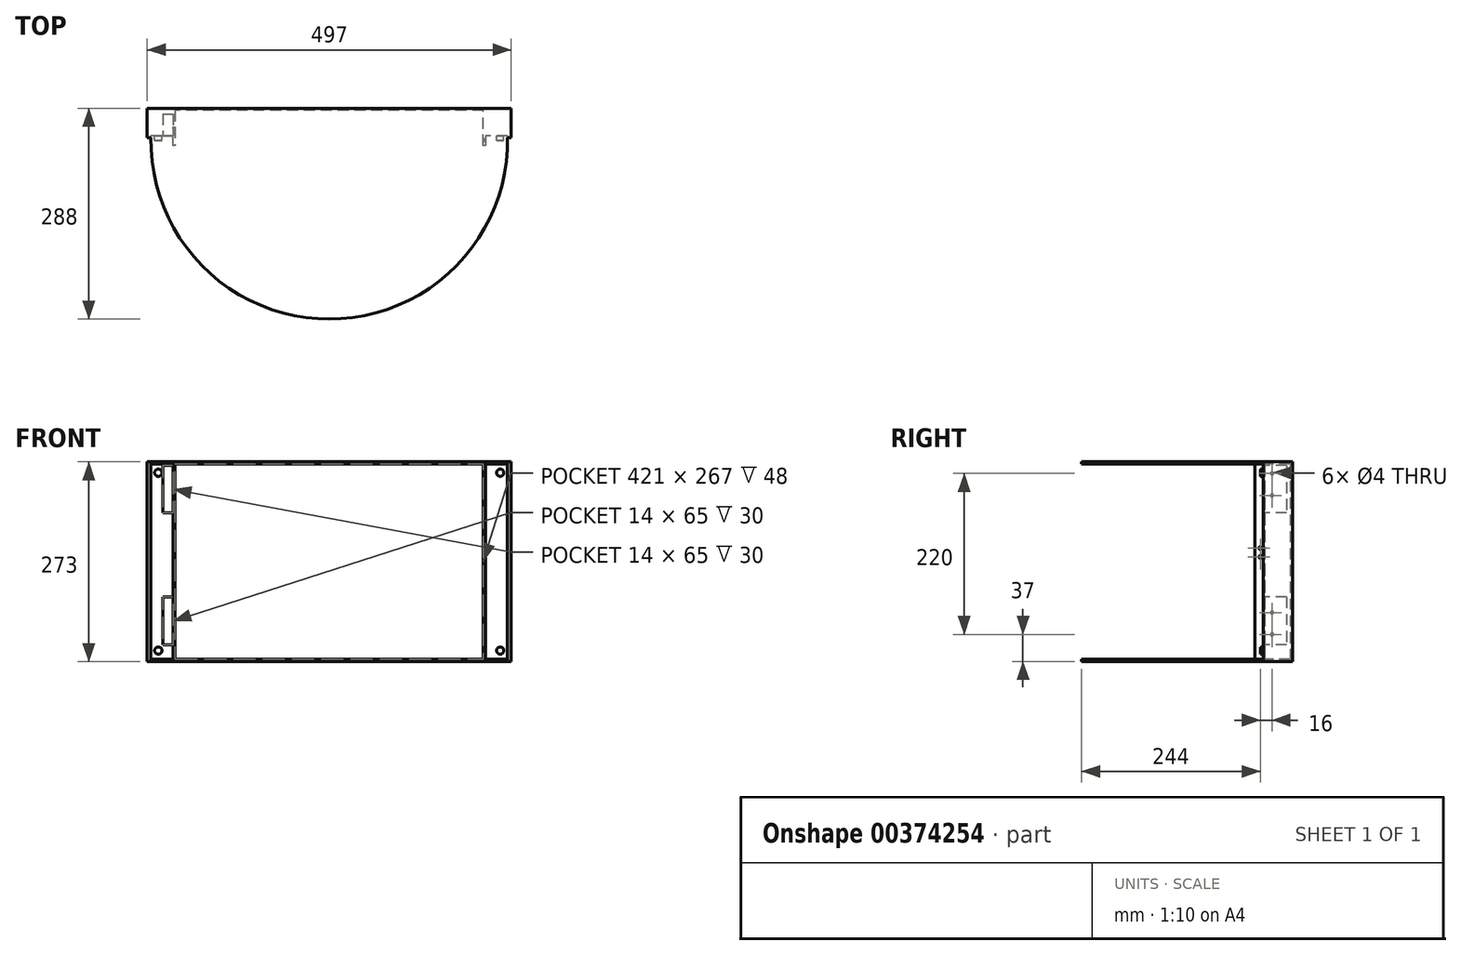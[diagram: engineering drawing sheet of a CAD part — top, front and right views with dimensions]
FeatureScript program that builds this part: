
annotation { "Feature Type Name" : "Feature", "Feature Type Description" : "" }
export const myFeature = defineFeature(function(context is Context, id is Id, definition is map)
    precondition{}
    {
        {
            var Q0;
            Q0=qCreatedBy(makeId("Top.planeOp"),FACE);
            var sketch = newSketch(context, id + "F0", { "sketchPlane" : qUnion([Q0])});
            skLineSegment(sketch, "E0", {"start": v(-248.5, 40) * mm, "end": v(248.5, 40) * mm});
            skLineSegment(sketch, "E1", {"start": v(248.5, 40) * mm, "end": v(248.5, 0) * mm});
            skLineSegment(sketch, "E2", {"start": v(248.5, 0) * mm, "end": v(243.5, 0) * mm});
            skLineSegment(sketch, "E3", {"start": v(243.5, 0) * mm, "end": v(243.5, 2) * mm});
            skLineSegment(sketch, "E4", {"start": v(243.5, 2) * mm, "end": v(213.5, 2) * mm});
            skLineSegment(sketch, "E5", {"start": v(213.5, 2) * mm, "end": v(213.5, -11) * mm});
            skLineSegment(sketch, "E6", {"start": v(213.5, -11) * mm, "end": v(210.5, -11) * mm});
            skLineSegment(sketch, "E7", {"start": v(210.5, -11) * mm, "end": v(210.5, 37) * mm});
            skLineSegment(sketch, "E8", {"start": v(210.5, 37) * mm, "end": v(-210.5, 37) * mm});
            skLineSegment(sketch, "E9", {"start": v(-210.5, 37) * mm, "end": v(-210.5, -11) * mm});
            skLineSegment(sketch, "E10", {"start": v(-210.5, -11) * mm, "end": v(-213.5, -11) * mm});
            skLineSegment(sketch, "E11", {"start": v(-213.5, -11) * mm, "end": v(-213.5, 2) * mm});
            skLineSegment(sketch, "E12", {"start": v(-213.5, 2) * mm, "end": v(-243.5, 2) * mm});
            skLineSegment(sketch, "E13", {"start": v(-243.5, 2) * mm, "end": v(-243.5, 0) * mm});
            skLineSegment(sketch, "E14", {"start": v(-243.5, 0) * mm, "end": v(-248.5, 0) * mm});
            skLineSegment(sketch, "E15", {"start": v(-248.5, 0) * mm, "end": v(-248.5, 40) * mm});
            skArc(sketch, "E16", {"start": v(-243.5, 0) * mm, "mid": v(0, -248) * mm, "end": v(243.5, 0) * mm});
            skSolve(sketch);
        }
        {
            var Q0;
            Q0=makeQuery(id+"F0.imprint","IMPRINT",FACE,{"disambiguationData":[TD([[makeQuery(id+"F0.imprint","IMPRINT",EDGE,{"derivedFrom":sQuery(id+"F0.wireOp",EDGE,"E3")}),1.0]])]});
            extrude(context, id + "F1", {"entities" : qUnion([Q0]), "depth" : 3 * mm});
        }
        {
            var Q0;
            Q0=makeQuery(id+"F0.imprint","IMPRINT",FACE,{"disambiguationData":[TD([[makeQuery(id+"F0.imprint","IMPRINT",EDGE,{"derivedFrom":sQuery(id+"F0.wireOp",EDGE,"E0")}),-1.0]])]});
            extrude(context, id + "F2", {"entities" : qUnion([Q0]), "operationType" : NewBodyOperationType.ADD, "depth" : 273 * mm});
        }
        {
            var Q0;
            Q0=makeQuery(id+"F1.opExtrude","CAP_FACE",FACE,{"disambiguationData":[OSD([sQuery(id+"F0.wireOp",EDGE,"E3"),sQuery(id+"F0.wireOp",EDGE,"E4"),sQuery(id+"F0.wireOp",EDGE,"E5"),sQuery(id+"F0.wireOp",EDGE,"E6"),sQuery(id+"F0.wireOp",EDGE,"E7"),sQuery(id+"F0.wireOp",EDGE,"E8"),sQuery(id+"F0.wireOp",EDGE,"E9"),sQuery(id+"F0.wireOp",EDGE,"E10"),sQuery(id+"F0.wireOp",EDGE,"E11"),sQuery(id+"F0.wireOp",EDGE,"E12"),sQuery(id+"F0.wireOp",EDGE,"E13"),sQuery(id+"F0.wireOp",EDGE,"E16")])],"isStart":false});
            extrude(context, id + "F3", {"entities" : qUnion([Q0]), "operationType" : NewBodyOperationType.ADD, "depth" : 270 * mm, "hasSecondDirection" : true, "secondDirectionOppositeDirection" : false, "secondDirectionDepth" : 267 * mm});
        }
        {
            var Q0;
            Q0=makeQuery(id+"F2.opExtrude","SWEPT_FACE",FACE,{"disambiguationData":[OSD([sQuery(id+"F0.wireOp",EDGE,"E12")])]});
            var sketch = newSketch(context, id + "F4", { "sketchPlane" : qUnion([Q0])});
            skLineSegment(sketch, "E17.bottom", {"start": v(-227.5, 88) * mm, "end": v(-213.5, 88) * mm});
            skLineSegment(sketch, "E17.top", {"start": v(-227.5, 23) * mm, "end": v(-213.5, 23) * mm});
            skLineSegment(sketch, "E17.left", {"start": v(-227.5, 88) * mm, "end": v(-227.5, 23) * mm});
            skLineSegment(sketch, "E17.right", {"start": v(-213.5, 88) * mm, "end": v(-213.5, 23) * mm});
            skLineSegment(sketch, "E18.bottom", {"start": v(-227.5, 268) * mm, "end": v(-213.5, 268) * mm});
            skLineSegment(sketch, "E18.top", {"start": v(-227.5, 203) * mm, "end": v(-213.5, 203) * mm});
            skLineSegment(sketch, "E18.left", {"start": v(-227.5, 268) * mm, "end": v(-227.5, 203) * mm});
            skLineSegment(sketch, "E18.right", {"start": v(-213.5, 268) * mm, "end": v(-213.5, 203) * mm});
            skCircle(sketch, "E19", {"center": v(-233.5, 258) * mm, "radius": 5 * mm});
            skCircle(sketch, "E20", {"center": v(-233.5, 15) * mm, "radius": 5 * mm});
            skCircle(sketch, "E21", {"center": v(233.5, 15) * mm, "radius": 5 * mm});
            skCircle(sketch, "E22", {"center": v(233.5, 258) * mm, "radius": 5 * mm});
            skSolve(sketch);
        }
        {
            var Q0;
            Q0=makeQuery(id+"F4.imprint","IMPRINT",FACE,{"disambiguationData":[TD([[makeQuery(id+"F4.imprint","IMPRINT",EDGE,{"derivedFrom":sQuery(id+"F4.wireOp",EDGE,"E18.bottom")}),-1.0]])]});
            var Q1;
            Q1=makeQuery(id+"F4.imprint","IMPRINT",FACE,{"disambiguationData":[TD([[makeQuery(id+"F4.imprint","IMPRINT",EDGE,{"derivedFrom":sQuery(id+"F4.wireOp",EDGE,"E17.bottom")}),-1.0]])]});
            extrude(context, id + "F5", {"entities" : qUnion([Q0, Q1]), "operationType" : NewBodyOperationType.REMOVE, "oppositeDirection" : true, "depth" : 30 * mm});
        }
        {
            var Q0;
            Q0=makeQuery(id+"F2.opExtrude","SWEPT_FACE",FACE,{"disambiguationData":[OSD([sQuery(id+"F0.wireOp",EDGE,"E9")])]});
            var sketch = newSketch(context, id + "F6", { "sketchPlane" : qUnion([Q0])});
            skPoint(sketch, "E23", {"position": v(12, 257) * mm});
            skPoint(sketch, "E24", {"position": v(12, 227) * mm});
            skPoint(sketch, "E25", {"position": v(12, 67) * mm});
            skPoint(sketch, "E26", {"position": v(12, 37) * mm});
            skSolve(sketch);
        }
        {
            var Q0;
            Q0=sQuery(id+"F6.wireOp",VERTEX,"E23");
            var Q1;
            Q1=sQuery(id+"F6.wireOp",VERTEX,"E24");
            var Q2;
            Q2=sQuery(id+"F6.wireOp",VERTEX,"E26");
            var Q3;
            Q3=sQuery(id+"F6.wireOp",VERTEX,"E25");
            var Q4;
            Q4=makeQuery(id+"F1.opExtrude","SWEPT_BODY",BODY,{"disambiguationData":[OSD([sQuery(id+"F0.wireOp",EDGE,"E3"),sQuery(id+"F0.wireOp",EDGE,"E4"),sQuery(id+"F0.wireOp",EDGE,"E5"),sQuery(id+"F0.wireOp",EDGE,"E6"),sQuery(id+"F0.wireOp",EDGE,"E7"),sQuery(id+"F0.wireOp",EDGE,"E8"),sQuery(id+"F0.wireOp",EDGE,"E9"),sQuery(id+"F0.wireOp",EDGE,"E10"),sQuery(id+"F0.wireOp",EDGE,"E11"),sQuery(id+"F0.wireOp",EDGE,"E12"),sQuery(id+"F0.wireOp",EDGE,"E13"),sQuery(id+"F0.wireOp",EDGE,"E16")])]});
            hole(context, id + "F7", {"style" : HoleStyle.SIMPLE, "endStyle" : HoleEndStyle.BLIND, "holeDiameter" : 4 * mm, "holeDepth" : 8 * mm, "isTappedThrough" : true, "tappedDepth" : 12 * mm, "tapClearance" : 3, "locations" : qUnion([Q0, Q1, Q2, Q3]), "scope" : qUnion([Q4])});
        }
        {
            var Q0;
            Q0=makeQuery(id+"F2.opExtrude","SWEPT_FACE",FACE,{"disambiguationData":[OSD([sQuery(id+"F0.wireOp",EDGE,"E7")])]});
            var sketch = newSketch(context, id + "F8", { "sketchPlane" : qUnion([Q0])});
            skPoint(sketch, "E27", {"position": v(4, 155) * mm});
            skPoint(sketch, "E28", {"position": v(4, 143) * mm});
            skSolve(sketch);
        }
        {
            var Q0;
            Q0=sQuery(id+"F8.wireOp",VERTEX,"E27");
            var Q1;
            Q1=sQuery(id+"F8.wireOp",VERTEX,"E28");
            var Q2;
            Q2=makeQuery(id+"F1.opExtrude","SWEPT_BODY",BODY,{"disambiguationData":[OSD([sQuery(id+"F0.wireOp",EDGE,"E3"),sQuery(id+"F0.wireOp",EDGE,"E4"),sQuery(id+"F0.wireOp",EDGE,"E5"),sQuery(id+"F0.wireOp",EDGE,"E6"),sQuery(id+"F0.wireOp",EDGE,"E7"),sQuery(id+"F0.wireOp",EDGE,"E8"),sQuery(id+"F0.wireOp",EDGE,"E9"),sQuery(id+"F0.wireOp",EDGE,"E10"),sQuery(id+"F0.wireOp",EDGE,"E11"),sQuery(id+"F0.wireOp",EDGE,"E12"),sQuery(id+"F0.wireOp",EDGE,"E13"),sQuery(id+"F0.wireOp",EDGE,"E16")])]});
            hole(context, id + "F9", {"style" : HoleStyle.SIMPLE, "endStyle" : HoleEndStyle.BLIND, "holeDiameter" : 4 * mm, "holeDepth" : 8 * mm, "isTappedThrough" : true, "tappedDepth" : 12 * mm, "tapClearance" : 3, "locations" : qUnion([Q0, Q1]), "scope" : qUnion([Q2])});
        }
        {
            var Q0;
            Q0=makeQuery(id+"F4.imprint","IMPRINT",FACE,{"disambiguationData":[TD([[makeQuery(id+"F4.imprint","IMPRINT",EDGE,{"derivedFrom":sQuery(id+"F4.wireOp",EDGE,"E19")}),1.0]])]});
            var Q1;
            Q1=makeQuery(id+"F4.imprint","IMPRINT",FACE,{"disambiguationData":[TD([[makeQuery(id+"F4.imprint","IMPRINT",EDGE,{"derivedFrom":sQuery(id+"F4.wireOp",EDGE,"E20")}),1.0]])]});
            var Q2;
            Q2=makeQuery(id+"F4.imprint","IMPRINT",FACE,{"disambiguationData":[TD([[makeQuery(id+"F4.imprint","IMPRINT",EDGE,{"derivedFrom":sQuery(id+"F4.wireOp",EDGE,"E21")}),1.0]])]});
            var Q3;
            Q3=makeQuery(id+"F4.imprint","IMPRINT",FACE,{"disambiguationData":[TD([[makeQuery(id+"F4.imprint","IMPRINT",EDGE,{"derivedFrom":sQuery(id+"F4.wireOp",EDGE,"E22")}),1.0]])]});
            extrude(context, id + "F10", {"entities" : qUnion([Q0, Q1, Q2, Q3]), "operationType" : NewBodyOperationType.ADD, "depth" : 6 * mm});
        }
    });
